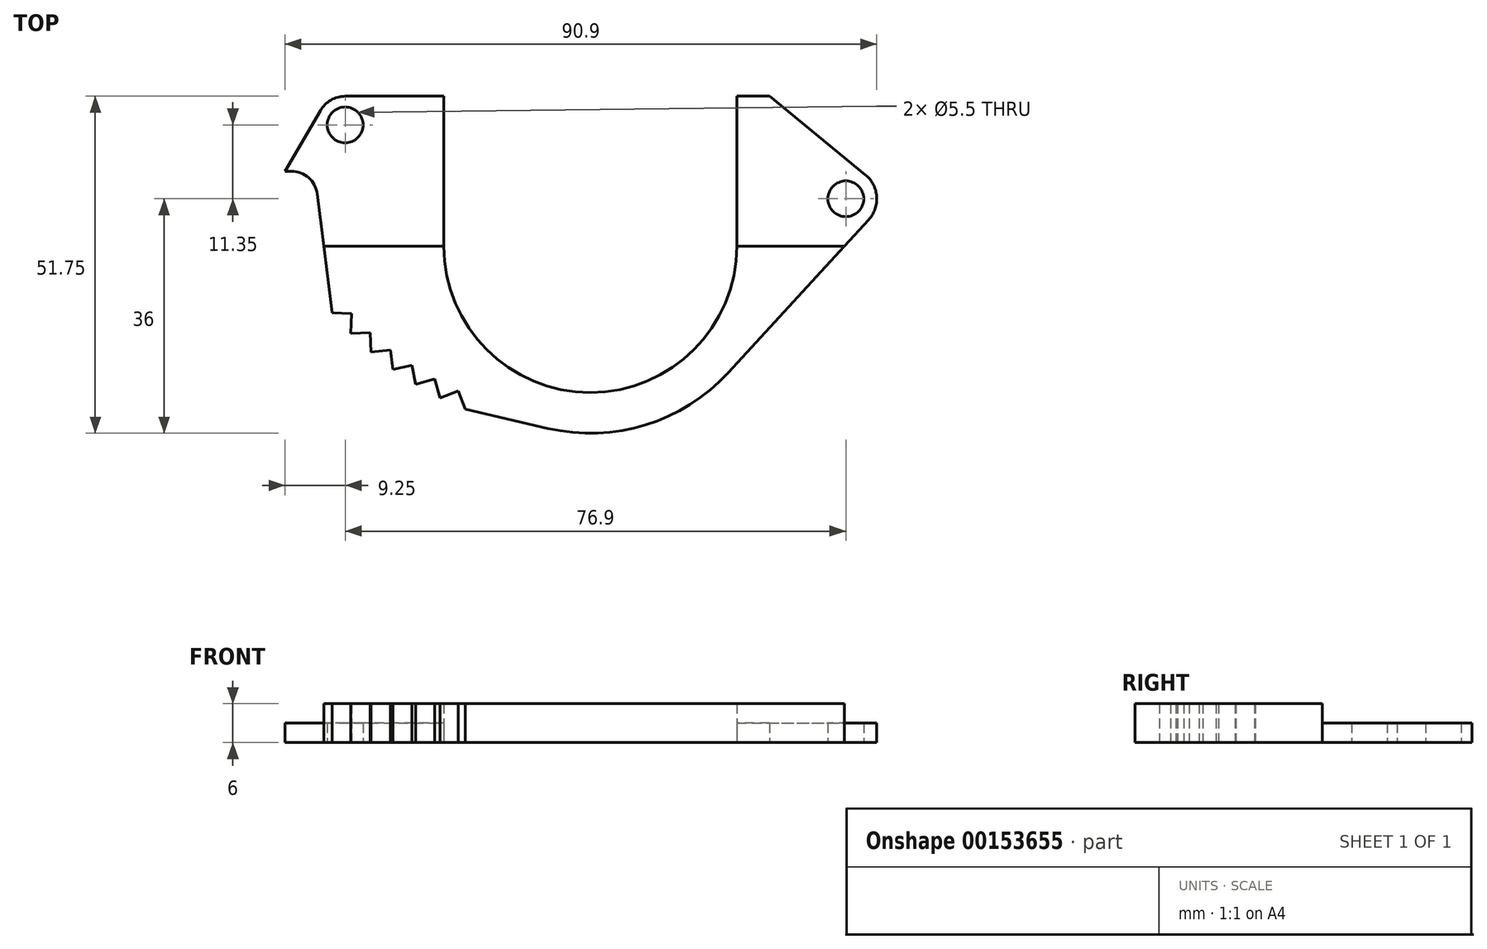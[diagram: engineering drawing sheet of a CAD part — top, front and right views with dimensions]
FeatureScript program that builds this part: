
annotation { "Feature Type Name" : "Feature", "Feature Type Description" : "" }
export const myFeature = defineFeature(function(context is Context, id is Id, definition is map)
    precondition{}
    {
        {
            var Q0;
            Q0=qCreatedBy(makeId("Top.planeOp"),FACE);
            var sketch = newSketch(context, id + "F0", { "sketchPlane" : qUnion([Q0])});
            skArc(sketch, "E0", {"start": v(-22.5, 0) * mm, "mid": v(0, -22.5) * mm, "end": v(22.5, 0) * mm});
            skArc(sketch, "E1.0", {"start": v(-28.75, 0) * mm, "mid": v(0, -28.75) * mm, "end": v(28.75, 0) * mm});
            skLineSegment(sketch, "E2", {"start": v(-22.5, 0) * mm, "end": v(-28.75, 0) * mm});
            skLineSegment(sketch, "E3", {"start": v(22.5, 0) * mm, "end": v(28.75, 0) * mm});
            skPoint(sketch, "E4", {"position": v(0, 23) * mm});
            skLineSegment(sketch, "E5", {"start": v(-22.5, 0) * mm, "end": v(-22.5, 23) * mm});
            skLineSegment(sketch, "E6", {"start": v(22.5, 0) * mm, "end": v(22.5, 23) * mm});
            skLineSegment(sketch, "E7", {"start": v(-28.75, 0) * mm, "end": v(-28.75, 23) * mm});
            skLineSegment(sketch, "E8", {"start": v(-28.75, 23) * mm, "end": v(-22.5, 23) * mm});
            skLineSegment(sketch, "E9", {"start": v(28.75, 0) * mm, "end": v(28.75, 21.98) * mm});
            skLineSegment(sketch, "E10", {"start": v(27.5, 23) * mm, "end": v(22.5, 23) * mm});
            skCircle(sketch, "E11", {"center": v(39.25, 7.25) * mm, "radius": 2.75 * mm});
            skCircle(sketch, "E12", {"center": v(39.25, 7.25) * mm, "radius": 4.75 * mm});
            skCircle(sketch, "E13", {"center": v(-37.65, 18.6) * mm, "radius": 2.75 * mm});
            skCircle(sketch, "E14", {"center": v(-37.65, 18.6) * mm, "radius": 4.4 * mm});
            skLineSegment(sketch, "E15", {"start": v(-28.75, 23) * mm, "end": v(-37.65, 23) * mm});
            skLineSegment(sketch, "E16", {"start": v(-46.9, 23) * mm, "end": v(-46.9, 2.46) * mm, "construction": true});
            skLineSegment(sketch, "E17", {"start": v(-49.68, 13.35) * mm, "end": v(-46.9, 13.35) * mm, "construction": true});
            skPoint(sketch, "E18", {"position": v(-46.9, 13.35) * mm});
            skArc(sketch, "E19", {"start": v(-46.9, 14.13) * mm, "mid": v(-46.9, 13.74) * mm, "end": v(-46.9, 13.35) * mm});
            skPoint(sketch, "E20", {"position": v(-40.5, 0) * mm});
            skLineSegment(sketch, "E21", {"start": v(-40.94, 0) * mm, "end": v(-28.75, 0) * mm});
            skLineSegment(sketch, "E22", {"start": v(-46.9, 13.35) * mm, "end": v(-41.62, 13.35) * mm});
            skPoint(sketch, "E23", {"position": v(27.5, 23) * mm});
            skLineSegment(sketch, "E24", {"start": v(27.5, 23) * mm, "end": v(42.26, 10.93) * mm});
            skPoint(sketch, "E25.orphan", {"position": v(28.75, 23) * mm});
            skArc(sketch, "E26", {"start": v(-39.64, -10.26) * mm, "mid": v(-30.34, -18.92) * mm, "end": v(-19.22, -25.05) * mm});
            skPoint(sketch, "E27", {"position": v(-19.42, -24.97) * mm});
            skLineSegment(sketch, "E28.bottom", {"start": v(-39.64, -10.26) * mm, "end": v(-36.64, -10.4) * mm});
            skLineSegment(sketch, "E29", {"start": v(-36.64, -10.4) * mm, "end": v(-36.78, -13.4) * mm});
            skLineSegment(sketch, "E30", {"start": v(-36.78, -13.4) * mm, "end": v(-33.78, -13.3) * mm});
            skLineSegment(sketch, "E31", {"start": v(-33.78, -13.3) * mm, "end": v(-33.67, -16.3) * mm});
            skPoint(sketch, "E32.start.orphan", {"position": v(-36.78, -15.96) * mm});
            skLineSegment(sketch, "E33", {"start": v(-33.67, -16.3) * mm, "end": v(-30.7, -15.94) * mm});
            skLineSegment(sketch, "E34", {"start": v(-30.7, -15.94) * mm, "end": v(-30.34, -18.92) * mm});
            skLineSegment(sketch, "E35", {"start": v(-30.34, -18.92) * mm, "end": v(-27.4, -18.32) * mm});
            skLineSegment(sketch, "E36", {"start": v(-27.4, -18.32) * mm, "end": v(-26.8, -21.26) * mm});
            skLineSegment(sketch, "E37", {"start": v(-26.8, -21.26) * mm, "end": v(-23.92, -20.43) * mm});
            skLineSegment(sketch, "E38", {"start": v(-23.92, -20.43) * mm, "end": v(-23.1, -23.31) * mm});
            skLineSegment(sketch, "E39", {"start": v(-23.1, -23.31) * mm, "end": v(-20.29, -22.24) * mm});
            skLineSegment(sketch, "E40", {"start": v(-20.29, -22.24) * mm, "end": v(-19.22, -25.05) * mm});
            skLineSegment(sketch, "E41", {"start": v(28.75, 0) * mm, "end": v(40.64, 0) * mm});
            skPoint(sketch, "E42.orphan", {"position": v(39.04, 0) * mm});
            skLineSegment(sketch, "E43", {"start": v(42.75, 4.04) * mm, "end": v(21.17, -19.45) * mm});
            skPoint(sketch, "E44.orphan", {"position": v(0, -28.75) * mm});
            skLineSegment(sketch, "E45", {"start": v(-19.22, -25.05) * mm, "end": v(-6.51, -28) * mm});
            skPoint(sketch, "E46", {"position": v(-46.9, 11.5) * mm});
            skLineSegment(sketch, "E47", {"start": v(-46.9, 11.5) * mm, "end": v(-41.45, 20.82) * mm});
            skLineSegment(sketch, "E48", {"start": v(-46.9, 11.5) * mm, "end": v(-45.92, 11.5) * mm});
            skLineSegment(sketch, "E49", {"start": v(-41.96, 8) * mm, "end": v(-39.64, -10.26) * mm});
            skLineSegment(sketch, "E50", {"start": v(-40.94, 0) * mm, "end": v(-22.5, 0) * mm});
            skPoint(sketch, "E51.visualSharp", {"position": v(-42.4, 11.5) * mm});
            skArc(sketch, "E51.filletArc", {"start": v(-41.96, 8) * mm, "mid": v(-43.28, 10.5) * mm, "end": v(-45.92, 11.5) * mm});
            skLineSegment(sketch, "E52", {"start": v(39.04, 0) * mm, "end": v(40.64, 0) * mm});
            skSolve(sketch);
        }
        {
            var Q0;
            {var subQ9=sQuery(id+"F0.wireOp",EDGE,"E7");Q0=makeQuery(id+"F0.imprint","IMPRINT",FACE,{"disambiguationData":[TD([[makeQuery(id+"F0.imprint","IMPRINT",EDGE,{"derivedFrom":subQ9}),1.0]])]});}
            var Q1;
            {var subQ0=sQuery(id+"F0.wireOp",EDGE,"E5");Q1=makeQuery(id+"F0.imprint","IMPRINT",FACE,{"disambiguationData":[TD([[makeQuery(id+"F0.imprint","IMPRINT",EDGE,{"derivedFrom":subQ0}),1.0]])]});}
            var Q2;
            Q2=makeQuery(id+"F0.imprint","IMPRINT",FACE,{"disambiguationData":[TD([[makeQuery(id+"F0.imprint","IMPRINT",EDGE,{"derivedFrom":sQuery(id+"F0.wireOp",EDGE,"E3")}),1.0]])]});
            var Q3;
            {var subQ2=sQuery(id+"F0.wireOp",EDGE,"E9");Q3=makeQuery(id+"F0.imprint","IMPRINT",FACE,{"disambiguationData":[TD([[makeQuery(id+"F0.imprint","IMPRINT",EDGE,{"derivedFrom":subQ2}),-1.0]])]});}
            var Q4;
            Q4=makeQuery(id+"F0.imprint","IMPRINT",FACE,{"disambiguationData":[TD([[makeQuery(id+"F0.imprint","IMPRINT",EDGE,{"derivedFrom":sQuery(id+"F0.wireOp",EDGE,"E11")}),-1.0]])]});
            var Q5;
            Q5=makeQuery(id+"F0.imprint","IMPRINT",FACE,{"disambiguationData":[TD([[makeQuery(id+"F0.imprint","IMPRINT",EDGE,{"derivedFrom":sQuery(id+"F0.wireOp",EDGE,"E13")}),-1.0]])]});
            extrude(context, id + "F1", {"entities" : qUnion([Q0, Q1, Q2, Q3, Q4, Q5]), "depth" : 3 * mm});
        }
        {
            var Q0;
            {var subQ0=sQuery(id+"F0.wireOp",EDGE,"E21");Q0=makeQuery(id+"F0.imprint","IMPRINT",FACE,{"disambiguationData":[TD([[makeQuery(id+"F0.imprint","IMPRINT",EDGE,{"derivedFrom":subQ0}),-1.0]])]});}
            var Q1;
            Q1=makeQuery(id+"F0.imprint","IMPRINT",FACE,{"disambiguationData":[TD([[makeQuery(id+"F0.imprint","IMPRINT",EDGE,{"derivedFrom":sQuery(id+"F0.wireOp",EDGE,"E0")}),-1.0]])]});
            var Q2;
            {var subQ0=sQuery(id+"F0.wireOp",EDGE,"E41");Q2=makeQuery(id+"F0.imprint","IMPRINT",FACE,{"disambiguationData":[TD([[makeQuery(id+"F0.imprint","IMPRINT",EDGE,{"derivedFrom":subQ0}),-1.0]])]});}
            var Q3;
            {var subQ0=sQuery(id+"F0.wireOp",EDGE,"E28.bottom");Q3=makeQuery(id+"F0.imprint","IMPRINT",FACE,{"disambiguationData":[TD([[makeQuery(id+"F0.imprint","IMPRINT",EDGE,{"derivedFrom":subQ0}),1.0]])]});}
            extrude(context, id + "F2", {"entities" : qUnion([Q0, Q1, Q2, Q3]), "depth" : 6 * mm});
        }
    });
